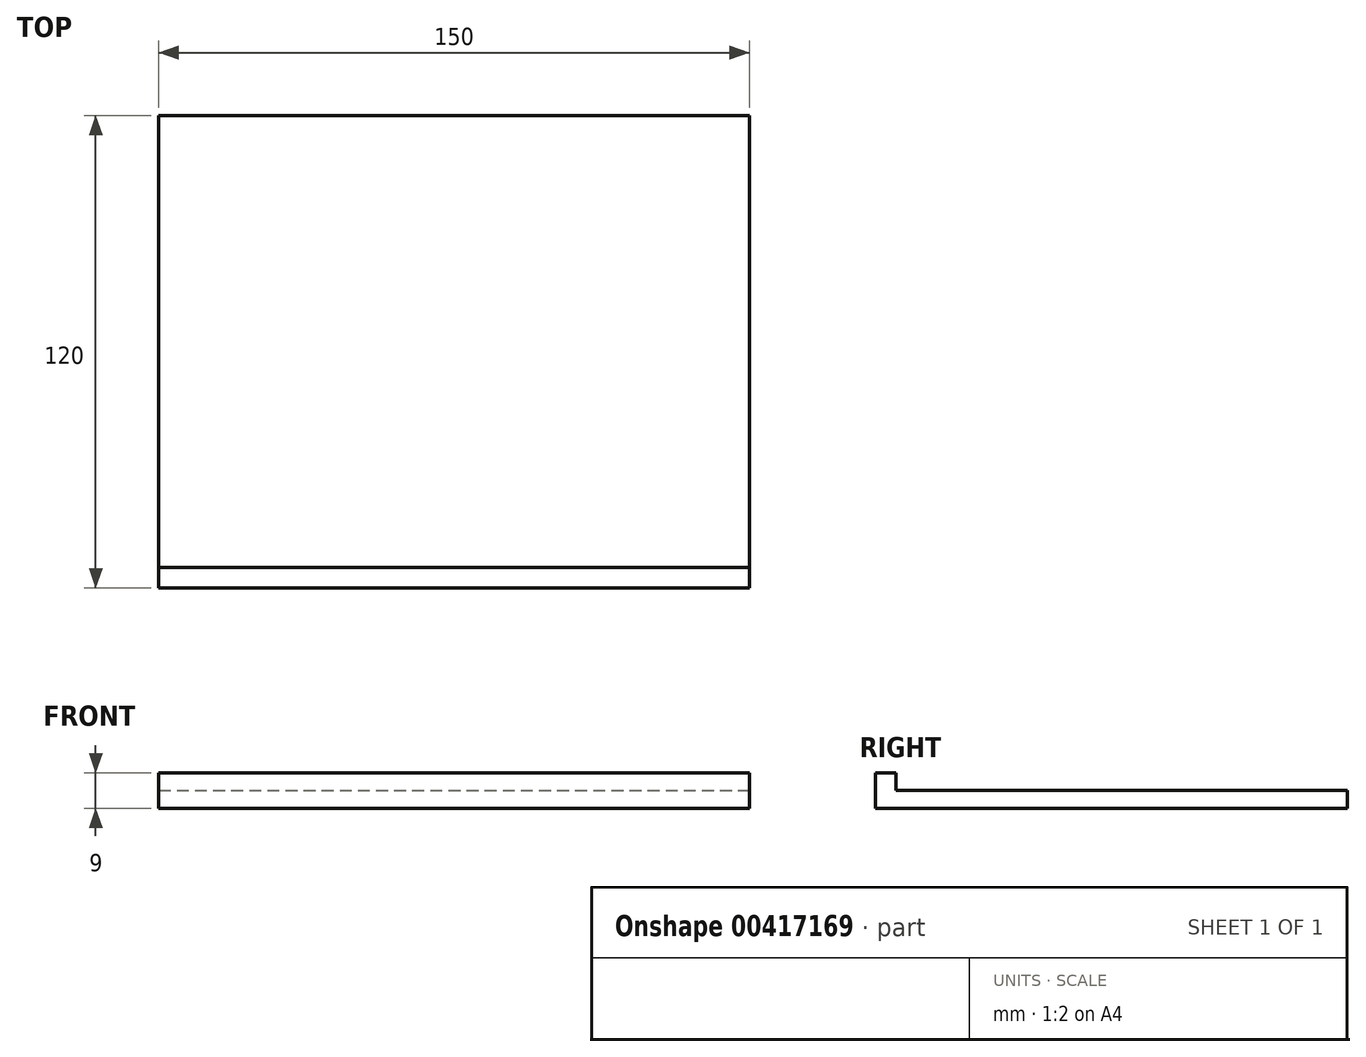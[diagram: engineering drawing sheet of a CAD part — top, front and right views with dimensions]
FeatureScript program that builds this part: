
annotation { "Feature Type Name" : "Feature", "Feature Type Description" : "" }
export const myFeature = defineFeature(function(context is Context, id is Id, definition is map)
    precondition{}
    {
        {
            var Q0;
            Q0=qCreatedBy(makeId("Top.planeOp"),FACE);
            var sketch = newSketch(context, id + "F0", { "sketchPlane" : qUnion([Q0])});
            skLineSegment(sketch, "E0.bottom", {"start": v(-75, 60) * mm, "end": v(75, 60) * mm});
            skLineSegment(sketch, "E0.top", {"start": v(-75, -60) * mm, "end": v(75, -60) * mm});
            skLineSegment(sketch, "E0.left", {"start": v(-75, 60) * mm, "end": v(-75, -60) * mm});
            skLineSegment(sketch, "E0.right", {"start": v(75, 60) * mm, "end": v(75, -60) * mm});
            skSolve(sketch);
        }
        {
            var Q0;
            Q0=makeQuery(id+"F0.imprint","IMPRINT",FACE,{"disambiguationData":[TD([[makeQuery(id+"F0.imprint","IMPRINT",EDGE,{"derivedFrom":sQuery(id+"F0.wireOp",EDGE,"E0.bottom")}),-1.0]])]});
            extrude(context, id + "F1", {"entities" : qUnion([Q0]), "depth" : 4.6 * mm});
        }
        {
            var Q0;
            Q0=makeQuery(id+"F1.opExtrude","CAP_FACE",FACE,{"disambiguationData":[OSD([sQuery(id+"F0.wireOp",EDGE,"E0.bottom"),sQuery(id+"F0.wireOp",EDGE,"E0.top"),sQuery(id+"F0.wireOp",EDGE,"E0.left"),sQuery(id+"F0.wireOp",EDGE,"E0.right")])],"isStart":false});
            var sketch = newSketch(context, id + "F2", { "sketchPlane" : qUnion([Q0])});
            skLineSegment(sketch, "E1.bottom", {"start": v(-75, -54.75) * mm, "end": v(75, -54.75) * mm});
            skLineSegment(sketch, "E1.top", {"start": v(-75, -60) * mm, "end": v(75, -60) * mm});
            skLineSegment(sketch, "E1.left", {"start": v(-75, -54.75) * mm, "end": v(-75, -60) * mm});
            skLineSegment(sketch, "E1.right", {"start": v(75, -54.75) * mm, "end": v(75, -60) * mm});
            skSolve(sketch);
        }
        {
            var Q0;
            Q0=makeQuery(id+"F2.imprint","IMPRINT",FACE,{"disambiguationData":[TD([[makeQuery(id+"F2.imprint","IMPRINT",EDGE,{"derivedFrom":sQuery(id+"F2.wireOp",EDGE,"E1.bottom")}),-1.0]])]});
            extrude(context, id + "F3", {"entities" : qUnion([Q0]), "operationType" : NewBodyOperationType.ADD, "depth" : (9 - 4.6) * mm});
        }
    });
